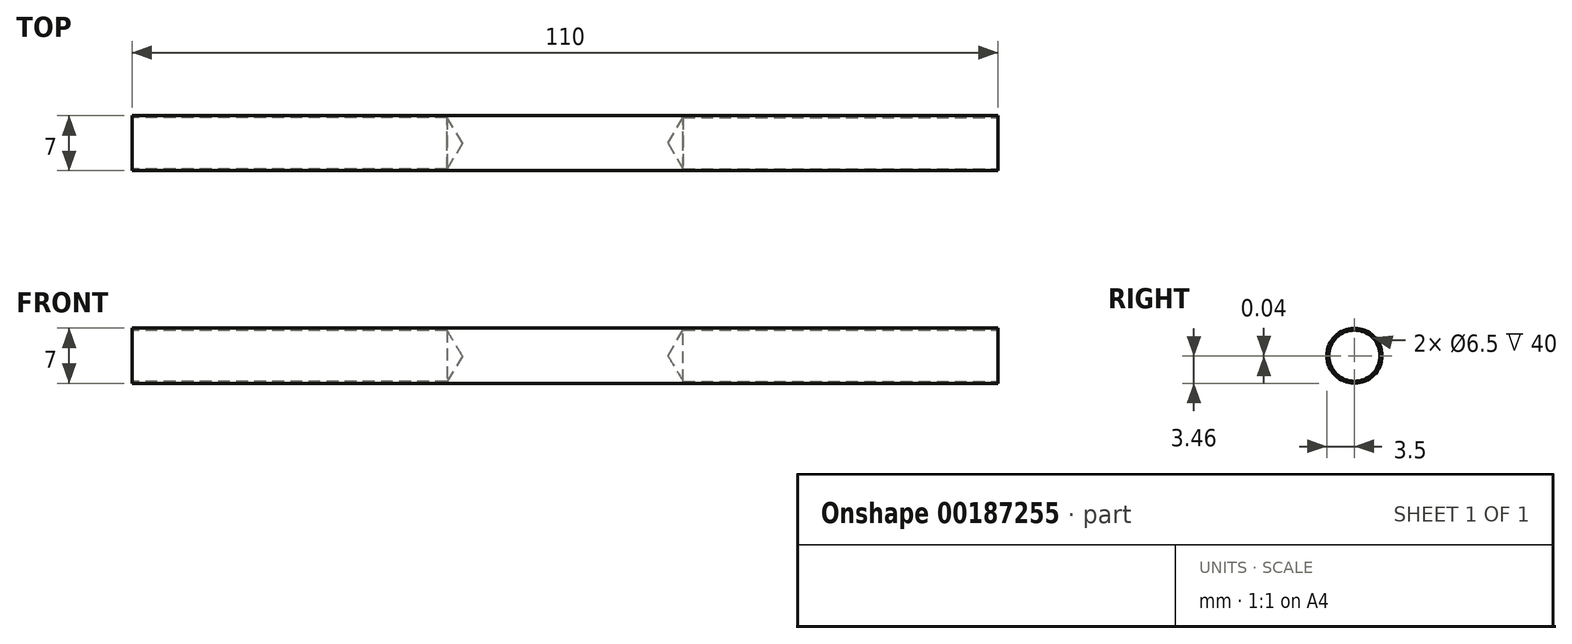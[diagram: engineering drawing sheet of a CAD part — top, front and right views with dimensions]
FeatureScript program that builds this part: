
annotation { "Feature Type Name" : "Feature", "Feature Type Description" : "" }
export const myFeature = defineFeature(function(context is Context, id is Id, definition is map)
    precondition{}
    {
        {
            var Q0;
            Q0=qCreatedBy(makeId("Top.planeOp"),FACE);
            var sketch = newSketch(context, id + "F0", { "sketchPlane" : qUnion([Q0])});
            skLineSegment(sketch, "E0.bottom", {"start": v(-55, 3.5) * mm, "end": v(55, 3.5) * mm});
            skLineSegment(sketch, "E0.top", {"start": v(-55, -3.5) * mm, "end": v(55, -3.5) * mm});
            skLineSegment(sketch, "E0.left", {"start": v(-55, 3.5) * mm, "end": v(-55, -3.5) * mm});
            skLineSegment(sketch, "E0.right", {"start": v(55, 3.5) * mm, "end": v(55, -3.5) * mm});
            skPoint(sketch, "E0.middle", {"position": v(0, 0) * mm});
            skSolve(sketch);
        }
        {
            var Q0;
            Q0=makeQuery(id+"F0.imprint","IMPRINT",FACE,{"disambiguationData":[TD([[makeQuery(id+"F0.imprint","IMPRINT",EDGE,{"derivedFrom":sQuery(id+"F0.wireOp",EDGE,"E0.bottom")}),-1.0]])]});
            extrude(context, id + "F1", {"entities" : qUnion([Q0]), "depth" : 7 * mm});
        }
        {
            var Q0;
            Q0=makeQuery(id+"F1.opExtrude","SWEPT_FACE",FACE,{"disambiguationData":[OSD([sQuery(id+"F0.wireOp",EDGE,"E0.left")])]});
            var sketch = newSketch(context, id + "F2", { "sketchPlane" : qUnion([Q0])});
            skLineSegment(sketch, "E1", {"start": v(-3.5, 3.5) * mm, "end": v(3.5, 3.5) * mm});
            skLineSegment(sketch, "E2", {"start": v(0, 0) * mm, "end": v(0, 7) * mm});
            skSolve(sketch);
        }
        {
            var Q0;
            Q0=makeQuery(id+"F1.opExtrude","CAP_EDGE",EDGE,{"disambiguationData":[OSD([sQuery(id+"F0.wireOp",EDGE,"E0.top")])],"isStart":false});
            var Q1;
            Q1=makeQuery(id+"F1.opExtrude","CAP_EDGE",EDGE,{"disambiguationData":[OSD([sQuery(id+"F0.wireOp",EDGE,"E0.bottom")])],"isStart":false});
            var Q2;
            Q2=makeQuery(id+"F1.opExtrude","CAP_EDGE",EDGE,{"disambiguationData":[OSD([sQuery(id+"F0.wireOp",EDGE,"E0.bottom")])],"isStart":true});
            var Q3;
            Q3=makeQuery(id+"F1.opExtrude","CAP_EDGE",EDGE,{"disambiguationData":[OSD([sQuery(id+"F0.wireOp",EDGE,"E0.top")])],"isStart":true});
            fillet(context, id + "F3", {"entities" : qUnion([Q0, Q1, Q2, Q3]), "radius" : 3.5 * mm, "tangentPropagation" : true, "allowEdgeOverflow" : false});
        }
        {
            var Q0;
            {var subQ1=sQuery(id+"F0.wireOp",EDGE,"E0.left");var subQ4=sQuery(id+"F2.wireOp",EDGE,"E2");var subQ6=makeQuery(id+"F1.opExtrude","CAP_EDGE",EDGE,{"disambiguationData":[OSD([subQ1])],"isStart":false});var subQ7=makeQuery(id+"F2.imprint","INTERSECT",VERTEX,{"derivedFrom":[subQ6,subQ4]});Q0=makeQuery(id+"F2.imprint","IMPRINT",FACE,{"disambiguationData":[TD([[makeQuery(id+"F2.imprint","IMPRINT",EDGE,{"disambiguationData":[TD([[subQ7,1.0]])],"derivedFrom":subQ4}),1.0]])]});}
            var sketch = newSketch(context, id + "F4", { "sketchPlane" : qUnion([Q0])});
            skCircle(sketch, "E3", {"center": v(0, 3.46) * mm, "radius": 3.25 * mm});
            skSolve(sketch);
        }
        {
            var Q0;
            Q0=makeQuery(id+"F1.opExtrude","SWEPT_FACE",FACE,{"disambiguationData":[OSD([sQuery(id+"F0.wireOp",EDGE,"E0.right")])]});
            var sketch = newSketch(context, id + "F5", { "sketchPlane" : qUnion([Q0])});
            skLineSegment(sketch, "E4", {"start": v(0, 3.5) * mm, "end": v(0, 0) * mm});
            skSolve(sketch);
        }
        {
            var Q0;
            Q0=sQuery(id+"F5.wireOp",VERTEX,"E4.start");
            var Q1;
            Q1=makeQuery(id+"F1.opExtrude","SWEPT_BODY",BODY,{"disambiguationData":[OSD([sQuery(id+"F0.wireOp",EDGE,"E0.bottom"),sQuery(id+"F0.wireOp",EDGE,"E0.top"),sQuery(id+"F0.wireOp",EDGE,"E0.left"),sQuery(id+"F0.wireOp",EDGE,"E0.right")])]});
            hole(context, id + "F6", {"style" : HoleStyle.SIMPLE, "endStyle" : HoleEndStyle.BLIND, "holeDiameter" : 6.5 * mm, "holeDepth" : 40 * mm, "locations" : qUnion([Q0]), "scope" : qUnion([Q1])});
        }
        {
            var Q0;
            Q0=sQuery(id+"F4.wireOp",VERTEX,"E3.center");
            var Q1;
            Q1=makeQuery(id+"F1.opExtrude","SWEPT_BODY",BODY,{"disambiguationData":[OSD([sQuery(id+"F0.wireOp",EDGE,"E0.bottom"),sQuery(id+"F0.wireOp",EDGE,"E0.top"),sQuery(id+"F0.wireOp",EDGE,"E0.left"),sQuery(id+"F0.wireOp",EDGE,"E0.right")])]});
            hole(context, id + "F7", {"style" : HoleStyle.SIMPLE, "endStyle" : HoleEndStyle.BLIND, "holeDiameter" : 6.5 * mm, "holeDepth" : 40 * mm, "locations" : qUnion([Q0]), "scope" : qUnion([Q1])});
        }
    });
